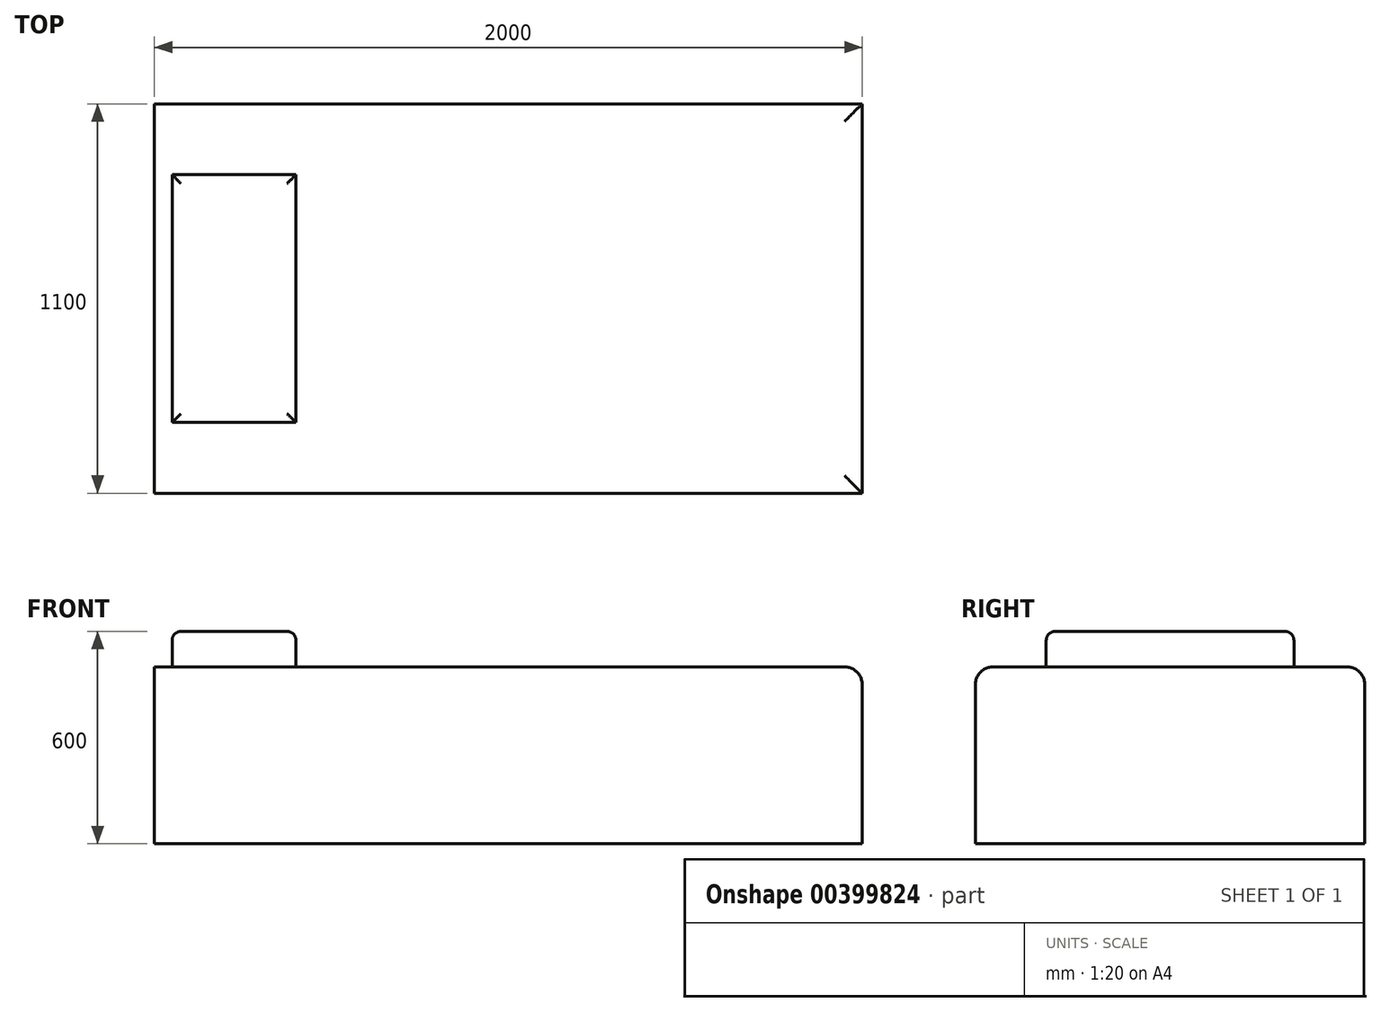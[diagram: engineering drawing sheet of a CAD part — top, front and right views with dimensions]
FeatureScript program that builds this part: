
annotation { "Feature Type Name" : "Feature", "Feature Type Description" : "" }
export const myFeature = defineFeature(function(context is Context, id is Id, definition is map)
    precondition{}
    {
        {
            var Q0;
            Q0=qCreatedBy(makeId("Top.planeOp"),FACE);
            var sketch = newSketch(context, id + "F0", { "sketchPlane" : qUnion([Q0])});
            skLineSegment(sketch, "E0.bottom", {"start": v(0, 0) * mm, "end": v(2000, 0) * mm});
            skLineSegment(sketch, "E0.top", {"start": v(0, 1100) * mm, "end": v(2000, 1100) * mm});
            skLineSegment(sketch, "E0.left", {"start": v(0, 0) * mm, "end": v(0, 1100) * mm});
            skLineSegment(sketch, "E0.right", {"start": v(2000, 0) * mm, "end": v(2000, 1100) * mm});
            skSolve(sketch);
        }
        {
            var Q0;
            Q0 = qSketchRegion(id + "F0", true);
            extrude(context, id + "F1", {"entities" : qUnion([Q0]), "depth" : 500 * mm});
        }
        {
            var Q0;
            Q0=makeQuery(id+"F1.opExtrude","CAP_FACE",FACE,{"disambiguationData":[OSD([sQuery(id+"F0.wireOp",EDGE,"E0.bottom"),sQuery(id+"F0.wireOp",EDGE,"E0.top"),sQuery(id+"F0.wireOp",EDGE,"E0.left"),sQuery(id+"F0.wireOp",EDGE,"E0.right")])],"isStart":false});
            var sketch = newSketch(context, id + "F2", { "sketchPlane" : qUnion([Q0])});
            skLineSegment(sketch, "E1.bottom", {"start": v(50, 200) * mm, "end": v(400, 200) * mm});
            skLineSegment(sketch, "E1.top", {"start": v(50, 900) * mm, "end": v(400, 900) * mm});
            skLineSegment(sketch, "E1.left", {"start": v(50, 200) * mm, "end": v(50, 900) * mm});
            skLineSegment(sketch, "E1.right", {"start": v(400, 200) * mm, "end": v(400, 900) * mm});
            skLineSegment(sketch, "E2", {"start": v(50, 900) * mm, "end": v(50, 1100) * mm, "construction": true});
            skLineSegment(sketch, "E3", {"start": v(50, 200) * mm, "end": v(50, 0) * mm, "construction": true});
            skSolve(sketch);
        }
        {
            var Q0;
            Q0 = qSketchRegion(id + "F2", true);
            extrude(context, id + "F3", {"entities" : qUnion([Q0]), "operationType" : NewBodyOperationType.ADD, "depth" : 100 * mm});
        }
        {
            var Q0;
            Q0=makeQuery(id+"F3.opExtrude","CAP_EDGE",EDGE,{"disambiguationData":[OSD([sQuery(id+"F2.wireOp",EDGE,"E1.bottom")])],"isStart":false});
            var Q1;
            Q1=makeQuery(id+"F3.opExtrude","CAP_FACE",FACE,{"disambiguationData":[OSD([sQuery(id+"F2.wireOp",EDGE,"E1.bottom"),sQuery(id+"F2.wireOp",EDGE,"E1.top"),sQuery(id+"F2.wireOp",EDGE,"E1.left"),sQuery(id+"F2.wireOp",EDGE,"E1.right")])],"isStart":false});
            fillet(context, id + "F4", {"entities" : qUnion([Q0, Q1]), "radius" : 25 * mm, "tangentPropagation" : true, "allowEdgeOverflow" : false});
        }
        {
            var Q0;
            Q0=makeQuery(id+"F1.opExtrude","CAP_EDGE",EDGE,{"disambiguationData":[OSD([sQuery(id+"F0.wireOp",EDGE,"E0.bottom")])],"isStart":false});
            var Q1;
            Q1=makeQuery(id+"F1.opExtrude","CAP_EDGE",EDGE,{"disambiguationData":[OSD([sQuery(id+"F0.wireOp",EDGE,"E0.right")])],"isStart":false});
            var Q2;
            Q2=makeQuery(id+"F1.opExtrude","CAP_EDGE",EDGE,{"disambiguationData":[OSD([sQuery(id+"F0.wireOp",EDGE,"E0.top")])],"isStart":false});
            fillet(context, id + "F5", {"entities" : qUnion([Q0, Q1, Q2]), "radius" : 50 * mm, "tangentPropagation" : true, "allowEdgeOverflow" : false});
        }
    });
